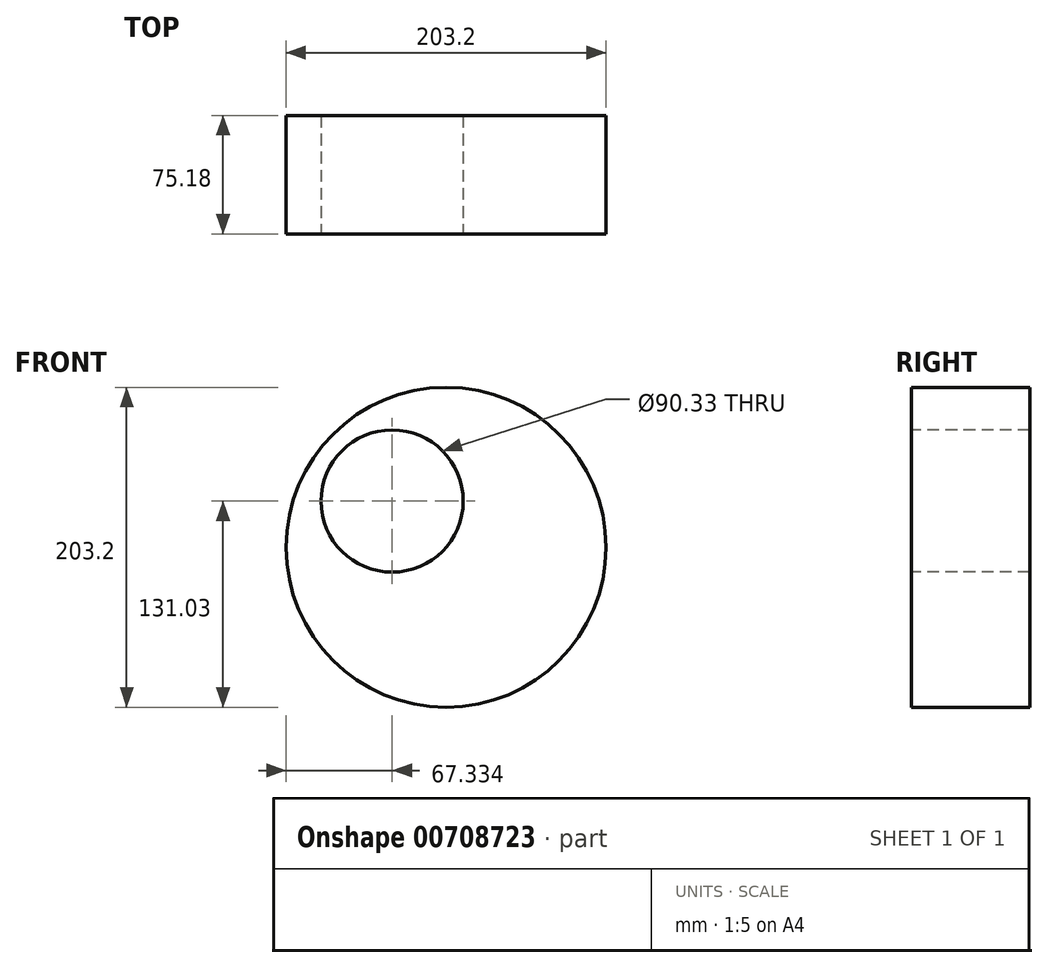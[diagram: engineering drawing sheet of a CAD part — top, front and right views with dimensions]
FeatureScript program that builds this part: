
annotation { "Feature Type Name" : "Feature", "Feature Type Description" : "" }
export const myFeature = defineFeature(function(context is Context, id is Id, definition is map)
    precondition{}
    {
        {
            var Q0;
            Q0=qCreatedBy(makeId("Front.planeOp"),FACE);
            var sketch = newSketch(context, id + "F0", { "sketchPlane" : qUnion([Q0])});
            skCircle(sketch, "E0", {"center": v(-12.12, 29.25) * mm, "radius": 45.17 * mm});
            skCircle(sketch, "E1", {"center": v(22.15, -0.18) * mm, "radius": 101.6 * mm});
            skSolve(sketch);
        }
        {
            var Q0;
            Q0=makeQuery(id+"F0.imprint","IMPRINT",FACE,{"disambiguationData":[TD([[makeQuery(id+"F0.imprint","IMPRINT",EDGE,{"derivedFrom":sQuery(id+"F0.wireOp",EDGE,"E0")}),-1.0]])]});
            extrude(context, id + "F1", {"entities" : qUnion([Q0]), "oppositeDirection" : true, "depth" : 75.18 * mm, "offsetDistance" : 25.4 * mm});
        }
    });
